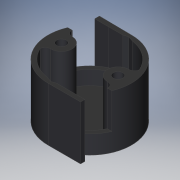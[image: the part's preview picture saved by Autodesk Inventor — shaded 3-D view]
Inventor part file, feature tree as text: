
AUTODESK INVENTOR PART (.ipt)
format: ipt  version: 2017 SP1 (Build 210196100, 196)  size: 242,688 bytes
history: native  units: mm
features: sketch x8, extrude x6, plane x2
ambient origin geometry x8: Origin, YZ Plane, XZ Plane, XY Plane, X Axis, Y Axis, Z Axis, Center Point
bodies: Solid1 (feature_tree)
feature tree (16):
  sketch  "Sketch1"  dims[d12=35.0mm d13=0.0mm d46=59.0mm]
  extrude  "Extrusion1"  Depth=35.0mm
  sketch  "Sketch9"  dims[d95=38.0mm d96=0.0mm d105=4.0mm]
  extrude  "Extrusion11"  Depth=6.75mm
  extrude  "Extrusion12"  Depth=3.0mm TaperAngle=0.0deg
  extrude  "Extrusion13"  Depth=25.0mm TaperAngle=0.0deg
  extrude  "Extrusion14"  Depth=10.0mm
  extrude  "Extrusion15"  Depth=4.0mm
  plane  "Work Plane2"
  sketch  "Sketch8"  dims[d93=10.0mm d94=10.0mm]
  plane  "Work Plane1"
  sketch  "Sketch6"  dims[d75=3.0mm d76=0.0mm d77=3.0mm d78=0.0mm]
  sketch  "Sketch2"  dims[d49=6.75mm d50=6.75mm]
  sketch  "Sketch7"  dims[d79=3.0mm d80=0.0mm d83=25.0mm d84=0.0mm]
  sketch  "Sketch10"  dims[d106=4.0mm]
  sketch  "Sketch11"  dims[d107=4.0mm d109=4.0mm]
